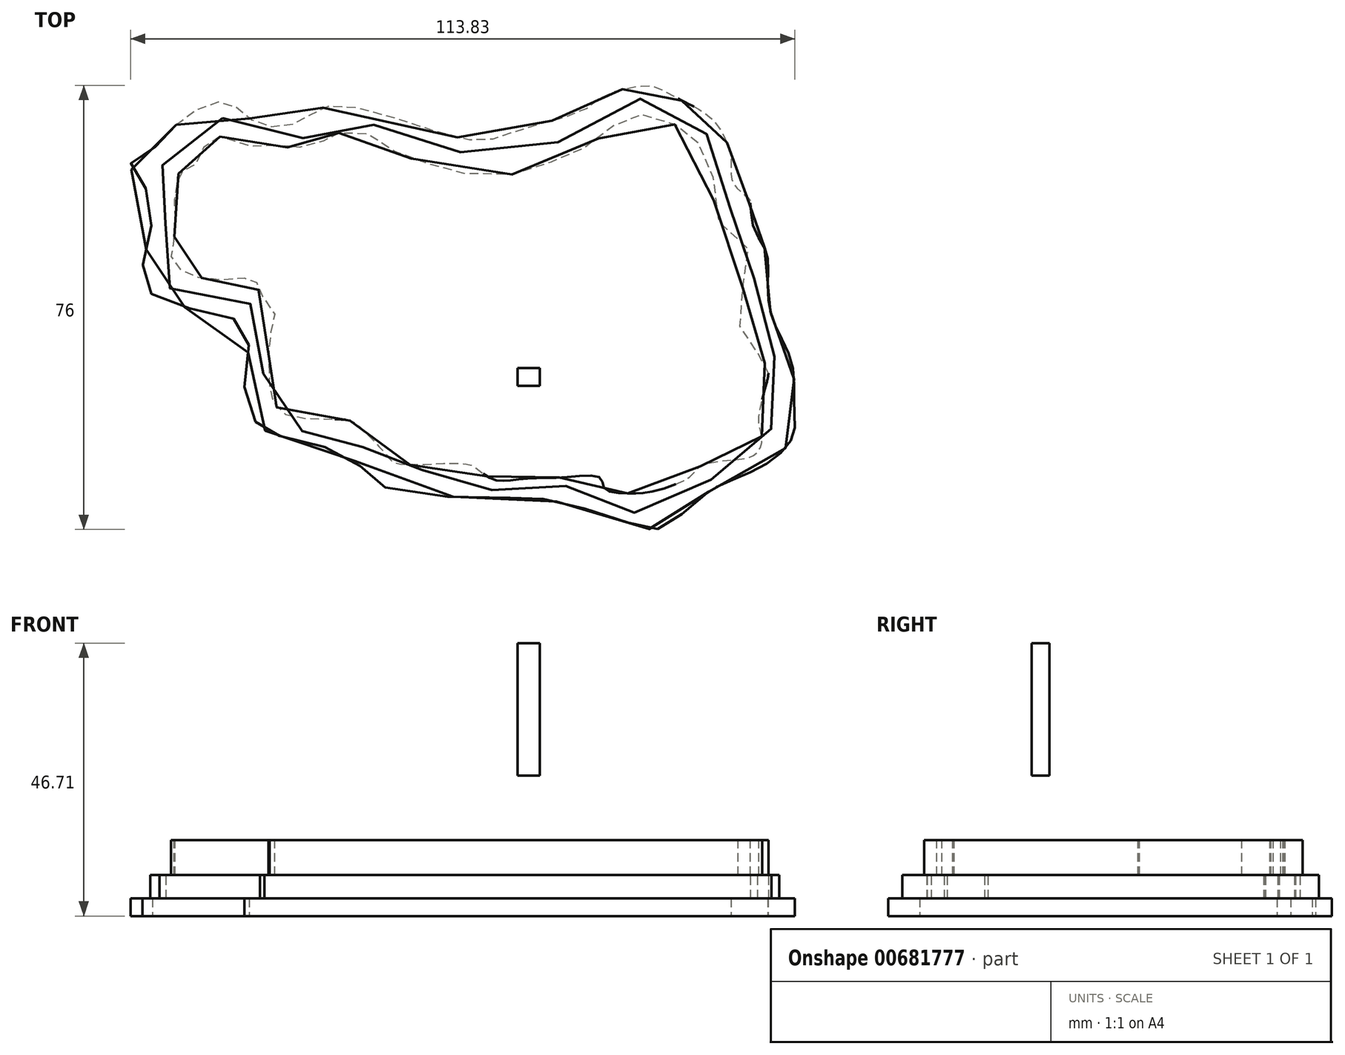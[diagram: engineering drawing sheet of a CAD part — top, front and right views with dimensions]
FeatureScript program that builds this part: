
annotation { "Feature Type Name" : "Feature", "Feature Type Description" : "" }
export const myFeature = defineFeature(function(context is Context, id is Id, definition is map)
    precondition{}
    {
        {
            var Q0;
            Q0=qCreatedBy(makeId("Top.planeOp"),FACE);
            var sketch = newSketch(context, id + "F0", { "sketchPlane" : qUnion([Q0])});
            skFitSpline(sketch, "E0", {"points": [v(-54.33, 41.7) * mm, v(-45.97, 45.6) * mm, v(-40.58, 42.07) * mm, v(-33.15, 42.25) * mm, v(-27.02, 45.04) * mm, v(-3.8, 39.1) * mm, v(4.36, 40.77) * mm, v(15.7, 44.3) * mm, v(18.67, 46.53) * mm, v(25.9, 48.38) * mm, v(28.14, 48.01) * mm, v(32.41, 45.78) * mm, v(36.68, 43.37) * mm, v(39.28, 40.21) * mm, v(40.77, 35.75) * mm, v(41.14, 31.67) * mm, v(43.74, 29.07) * mm, v(44.11, 27.95) * mm, v(44.67, 24.05) * mm, v(46.71, 20.15) * mm, v(47.08, 16.8) * mm, v(47.27, 10.68) * mm, v(48.94, 6.04) * mm, v(51.35, 0) * mm, v(51.54, -6.6) * mm, v(51.35, -11.6) * mm, v(46.15, -16.8) * mm, v(37.61, -20.7) * mm, v(31.67, -25.54) * mm, v(27.77, -27.58) * mm, v(21.64, -25.9) * mm, v(9.38, -22.57) * mm, v(2.88, -22.2) * mm, v(-19.6, -19.97) * mm, v(-23.87, -15.7) * mm, v(-35.75, -11.8) * mm, v(-40.4, -9.57) * mm, v(-42.63, -1.95) * mm, v(-42.25, 6.78) * mm, v(-51.35, 10.12) * mm, v(-59.53, 13.84) * mm, v(-59.34, 20.7) * mm, v(-58.97, 29.8) * mm, v(-62.13, 34.82) * mm, v(-58.23, 37.61) * mm, v(-54.33, 41.7) * mm]});
            skSolve(sketch);
        }
        {
            var Q0;
            Q0=makeQuery(id+"F0.imprint","IMPRINT",FACE,{"disambiguationData":[TD([[makeQuery(id+"F0.imprint","IMPRINT",EDGE,{"derivedFrom":sQuery(id+"F0.wireOp",EDGE,"E0")}),-1.0]])]});
            extrude(context, id + "F1", {"entities" : qUnion([Q0]), "depth" : 3 * mm, "offsetDistance" : 25 * mm});
        }
        {
            var Q0;
            Q0=qCreatedBy(makeId("Top.planeOp"),FACE);
            var sketch = newSketch(context, id + "F2", { "sketchPlane" : qUnion([Q0])});
            skFitSpline(sketch, "E1", {"points": [v(-46.34, 42.81) * mm, v(-49.87, 42.07) * mm, v(-53.4, 37.61) * mm, v(-56, 34.82) * mm, v(-58.6, 34.45) * mm, v(-58.04, 32.41) * mm, v(-56.37, 30.55) * mm, v(-56.18, 24.24) * mm, v(-56.56, 20.9) * mm, v(-57.11, 18.48) * mm, v(-56.56, 14.77) * mm, v(-54.33, 13.28) * mm, v(-48.75, 11.98) * mm, v(-44.48, 11.6) * mm, v(-41.14, 10.68) * mm, v(-39.84, 7.7) * mm, v(-39.28, 4.74) * mm, v(-39.28, 0) * mm, v(-39.65, -2.5) * mm, v(-39.84, -5.66) * mm, v(-37.05, -8.64) * mm, v(-31.3, -11.05) * mm, v(-29.62, -10.5) * mm, v(-24.8, -11.42) * mm, v(-23.68, -12.35) * mm, v(-21.64, -14.2) * mm, v(-19.78, -16.62) * mm, v(-16.62, -17.92) * mm, v(-13.28, -17.55) * mm, v(-9, -17.55) * mm, v(-4.18, -18.85) * mm, v(-3.8, -19.78) * mm, v(0, -20.9) * mm, v(4.18, -20.9) * mm, v(6.22, -20.9) * mm, v(8.82, -20.52) * mm, v(14.4, -20.34) * mm, v(15.5, -21.08) * mm, v(18.85, -22.57) * mm, v(23.12, -24.42) * mm, v(29.44, -24.8) * mm, v(33.15, -21.08) * mm, v(37.05, -19.22) * mm, v(43, -16.62) * mm, v(46.71, -14.4) * mm, v(47.64, -10.68) * mm, v(47.27, -7.34) * mm, v(48.38, -2.88) * mm, v(48.94, 0) * mm, v(47.08, 4) * mm, v(45.41, 7.34) * mm, v(44.11, 11.8) * mm, v(45.23, 17.55) * mm, v(45.04, 20.7) * mm, v(43.55, 23.12) * mm, v(40.4, 27.77) * mm, v(39.28, 32.6) * mm, v(38.72, 35.57) * mm, v(37.05, 39.28) * mm, v(34.08, 43.18) * mm, v(30.37, 45.23) * mm, v(26.65, 45.97) * mm, v(23.68, 46.15) * mm, v(20.7, 45.04) * mm, v(13.65, 40.21) * mm, v(6.22, 36.87) * mm, v(0, 37.05) * mm, v(-6.4, 37.05) * mm, v(-12.72, 38.54) * mm, v(-16.8, 40.21) * mm, v(-22.2, 42.07) * mm, v(-26.1, 42.07) * mm, v(-28.88, 42.07) * mm, v(-32.41, 39.47) * mm, v(-37.05, 39.47) * mm, v(-42.44, 39.84) * mm, v(-46.34, 42.81) * mm]});
            skSolve(sketch);
        }
        {
            var Q0;
            Q0 = qSketchRegion(id + "F2", true);
            extrude(context, id + "F3", {"entities" : qUnion([Q0]), "operationType" : NewBodyOperationType.ADD, "depth" : 7 * mm, "offsetDistance" : 25 * mm});
        }
        {
            var Q0;
            Q0=qCreatedBy(makeId("Top.planeOp"),FACE);
            var sketch = newSketch(context, id + "F4", { "sketchPlane" : qUnion([Q0])});
            skFitSpline(sketch, "E2", {"points": [v(-46.8, 39.65) * mm, v(-49.6, 37.8) * mm, v(-50.9, 35.01) * mm, v(-52.56, 33.9) * mm, v(-53.86, 33.34) * mm, v(-54.05, 32.22) * mm, v(-54.6, 29.07) * mm, v(-54.6, 27.58) * mm, v(-54.6, 22.57) * mm, v(-55.16, 20.15) * mm, v(-54.8, 17.92) * mm, v(-52.75, 16.44) * mm, v(-49.4, 15.32) * mm, v(-44.39, 15.32) * mm, v(-41.23, 15.32) * mm, v(-40.49, 14.58) * mm, v(-39.93, 12.9) * mm, v(-37.52, 9.57) * mm, v(-37.89, 7.15) * mm, v(-38.45, 2.88) * mm, v(-38.45, 0) * mm, v(-38.26, -2.32) * mm, v(-38.26, -4) * mm, v(-37.52, -6.04) * mm, v(-35.66, -7.9) * mm, v(-31.76, -8.64) * mm, v(-25.45, -8.82) * mm, v(-23.22, -9.75) * mm, v(-18.2, -14.95) * mm, v(-16.72, -16.25) * mm, v(-10.96, -16.44) * mm, v(-4.46, -16.44) * mm, v(-2.6, -17.37) * mm, v(0, -19.04) * mm, v(2.79, -19.22) * mm, v(6.87, -18.85) * mm, v(12.63, -18.67) * mm, v(18.39, -18.85) * mm, v(19.13, -20.7) * mm, v(23.22, -21.45) * mm, v(26.56, -21.27) * mm, v(33.62, -18.67) * mm, v(35.47, -16.8) * mm, v(41.05, -15.7) * mm, v(45.13, -14.58) * mm, v(46.06, -11.8) * mm, v(45.5, -9.2) * mm, v(46.99, -1.95) * mm, v(46.99, 0) * mm, v(45.13, 2.88) * mm, v(42.53, 6.6) * mm, v(42.35, 12.17) * mm, v(43.83, 20.15) * mm, v(38.63, 25.17) * mm, v(37.52, 34.45) * mm, v(34.36, 39.28) * mm, v(31.2, 41.7) * mm, v(25.63, 43.37) * mm, v(21.92, 42.44) * mm, v(16.72, 38.35) * mm, v(11.33, 35.94) * mm, v(5.2, 33.52) * mm, v(-5.01, 33.34) * mm, v(-11.14, 35.01) * mm, v(-17.09, 37.24) * mm, v(-21.17, 40.03) * mm, v(-25.45, 40.03) * mm, v(-27.3, 40.4) * mm, v(-28.6, 39.28) * mm, v(-30.65, 38.17) * mm, v(-33.8, 37.8) * mm, v(-36.59, 37.98) * mm, v(-40.12, 38.35) * mm, v(-41.79, 37.98) * mm, v(-46.8, 39.65) * mm]});
            skLineSegment(sketch, "E3", {"start": v(3.3, -15.14) * mm, "end": v(8.4, -15.14) * mm});
            skSolve(sketch);
        }
        {
            var Q0;
            Q0 = qSketchRegion(id + "F4", true);
            extrude(context, id + "F5", {"entities" : qUnion([Q0]), "operationType" : NewBodyOperationType.ADD, "depth" : 13 * mm, "offsetDistance" : 25 * mm});
        }
        {
            var Q0;
            Q0=qCreatedBy(makeId("Front.planeOp"),FACE);
            var sketch = newSketch(context, id + "F6", { "sketchPlane" : qUnion([Q0])});
            skLineSegment(sketch, "E4.bottom", {"start": v(4.15, 24.05) * mm, "end": v(7.98, 24.05) * mm});
            skLineSegment(sketch, "E4.top", {"start": v(4.15, 46.71) * mm, "end": v(7.98, 46.71) * mm});
            skLineSegment(sketch, "E4.left", {"start": v(4.15, 24.05) * mm, "end": v(4.15, 46.71) * mm});
            skLineSegment(sketch, "E4.right", {"start": v(7.98, 24.05) * mm, "end": v(7.98, 46.71) * mm});
            skSolve(sketch);
        }
        {
            var Q0;
            Q0=makeQuery(id+"F6.imprint","IMPRINT",FACE,{"disambiguationData":[TD([[makeQuery(id+"F6.imprint","IMPRINT",EDGE,{"derivedFrom":sQuery(id+"F6.wireOp",EDGE,"E4.bottom")}),1.0]])]});
            extrude(context, id + "F7", {"entities" : qUnion([Q0]), "depth" : 3 * mm, "offsetDistance" : 25 * mm});
        }
    });
